# Revit family: Light_Fixture-Wall_Sconce-KOHLER-Devonshire-K-10572
name_source: partatom
category: Lighting Fixtures
revit_build: Autodesk Revit 2015 (Build: 20140606_1530(x64)
units: mm (PartAtom-declared; Revit-internal decimal feet)

## types (5) — shared parameters
ADA Compliant = No
Apparent Load = 0 VA
Assembly Code = C1030200
Color Filter = 16777215
Date Modified = 12/12/2018
Default Elevation = 42"
Description = Triple wall sconce
Dimming Lamp Color Temperature Shift = Incandescent Lamp Curve
Electrical Connector = Yes
Emit from Line Length = 6"
Height = 9 1/8"
Lamp = CUL- and UL-approved up to 100 watts
Length = 23"
Light Source Symbol Size = 8"
Manufacturer = KOHLER Co.
MasterFormat 1995 = 10820
MasterFormat 2004 = 10.28.13
Material = Premium Metal Construction
Product Documentation Link = http://www.us.kohler.com
Product Name = Devonshire
Product Page URL = http://www.us.kohler.com
URL = https://www.us.kohler.com
Voltage = 120 V
Wattage Comments = Upto 100W
Width = 6"
zero-valued in all types: Cost

## per-type parameters (varying)
| type | Finish | Model | Type |
| CP-Polished Chrome | Kohler-Metal-CP-Polished_Chrome | K-10572-CP | 1 |
| SN-Vibrant Polished Nickel | Kohler-Metal-SN-Vibrant_Polished_Nickel | K-10572-SN | 2 |
| BN-Vibrant Brushed Nickel | Kohler-Metal-BN-Vibrant_Brushed_Nickel | K-10572-BN | 3 |
| BV-Vibrant Brushed Bronze | Kohler-Metal-BV-Brushed_Bronze | K-10572-BV | 4 |
| 2BZ-Oil-Rubbed Bronze | Kohler-Metal-2BZ-Oil_Rubbed_Bronze | K-10572-2BZ | 5 |

## geometry (parser evidence)
native form markers: Sweep x11
no freeform markers — native parametric forms only
